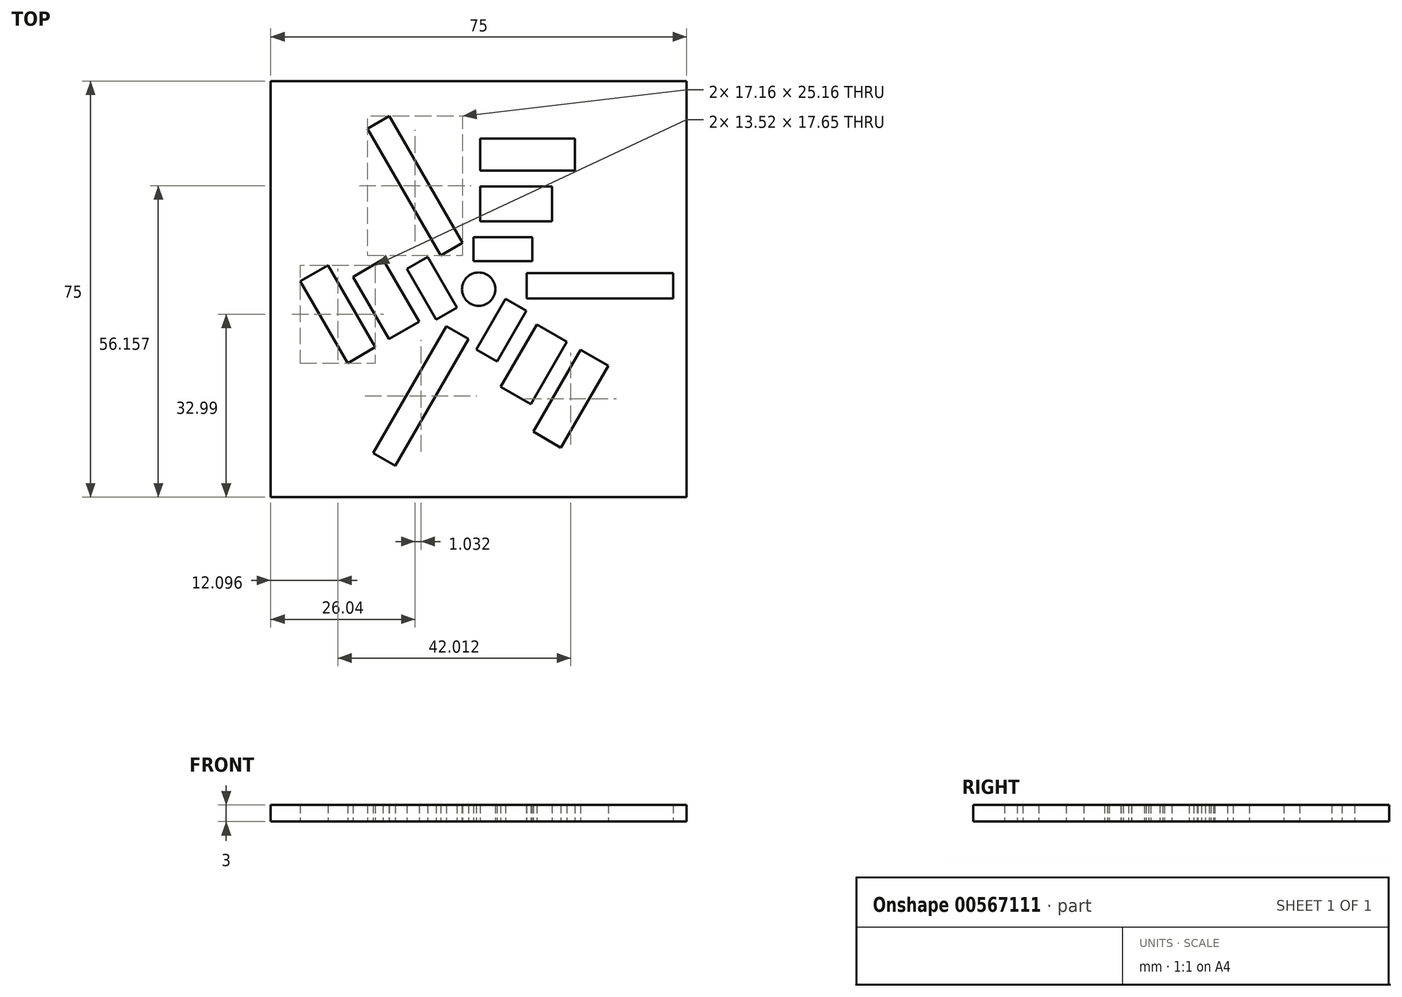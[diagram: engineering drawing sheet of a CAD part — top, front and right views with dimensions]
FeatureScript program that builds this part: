
annotation { "Feature Type Name" : "Feature", "Feature Type Description" : "" }
export const myFeature = defineFeature(function(context is Context, id is Id, definition is map)
    precondition{}
    {
        {
            var Q0;
            Q0=qCreatedBy(makeId("Top.planeOp"),FACE);
            var sketch = newSketch(context, id + "F0", { "sketchPlane" : qUnion([Q0])});
            skLineSegment(sketch, "E0.bottom", {"start": v(0, 0) * mm, "end": v(75, 0) * mm});
            skLineSegment(sketch, "E0.top", {"start": v(0, 75) * mm, "end": v(75, 75) * mm});
            skLineSegment(sketch, "E0.left", {"start": v(0, 0) * mm, "end": v(0, 75) * mm});
            skLineSegment(sketch, "E0.right", {"start": v(75, 0) * mm, "end": v(75, 75) * mm});
            skLineSegment(sketch, "E1", {"start": v(0, 75) * mm, "end": v(75, 0) * mm});
            skCircle(sketch, "E2", {"center": v(37.5, 37.5) * mm, "radius": 7.82 * mm});
            skSolve(sketch);
        }
        {
            var Q0;
            {var subQ1=sQuery(id+"F0.wireOp",EDGE,"E0.bottom");Q0=makeQuery(id+"F0.imprint","IMPRINT",FACE,{"disambiguationData":[TD([[makeQuery(id+"F0.imprint","IMPRINT",EDGE,{"derivedFrom":subQ1}),1.0]])]});}
            var sketch = newSketch(context, id + "F1", { "sketchPlane" : qUnion([Q0])});
            skLineSegment(sketch, "E3.bottom", {"start": v(0, 0) * mm, "end": v(-75, 0) * mm});
            skLineSegment(sketch, "E3.top", {"start": v(0, -75) * mm, "end": v(-75, -75) * mm});
            skLineSegment(sketch, "E3.left", {"start": v(0, 0) * mm, "end": v(0, -75) * mm});
            skLineSegment(sketch, "E3.right", {"start": v(-75, 0) * mm, "end": v(-75, -75) * mm});
            skLineSegment(sketch, "E4", {"start": v(-75, 0) * mm, "end": v(0, -75) * mm});
            skCircle(sketch, "E5", {"center": v(-37.5, -37.5) * mm, "radius": 3 * mm});
            skCircle(sketch, "E6", {"center": v(-37.5, -37.5) * mm, "radius": 37.5 * mm});
            skLineSegment(sketch, "E7.bottom", {"start": v(-38.43, -32.46) * mm, "end": v(-27.86, -32.46) * mm});
            skLineSegment(sketch, "E7.top", {"start": v(-38.43, -28.14) * mm, "end": v(-27.86, -28.14) * mm});
            skLineSegment(sketch, "E7.left", {"start": v(-38.43, -32.46) * mm, "end": v(-38.43, -28.14) * mm});
            skLineSegment(sketch, "E7.right", {"start": v(-27.86, -32.46) * mm, "end": v(-27.86, -28.14) * mm});
            skLineSegment(sketch, "E8.1.0", {"start": v(-45.14, -42.99) * mm, "end": v(-50.43, -33.84) * mm});
            skLineSegment(sketch, "E8.1.1", {"start": v(-46.68, -31.67) * mm, "end": v(-50.43, -33.84) * mm});
            skLineSegment(sketch, "E8.1.2", {"start": v(-41.4, -40.83) * mm, "end": v(-46.68, -31.67) * mm});
            skLineSegment(sketch, "E8.1.3", {"start": v(-41.4, -40.83) * mm, "end": v(-45.14, -42.99) * mm});
            skLineSegment(sketch, "E8.2.0", {"start": v(-28.93, -41.37) * mm, "end": v(-34.2, -50.53) * mm});
            skLineSegment(sketch, "E8.2.1", {"start": v(-37.95, -48.37) * mm, "end": v(-34.2, -50.53) * mm});
            skLineSegment(sketch, "E8.2.2", {"start": v(-32.67, -39.21) * mm, "end": v(-37.95, -48.37) * mm});
            skLineSegment(sketch, "E8.2.3", {"start": v(-32.67, -39.21) * mm, "end": v(-28.93, -41.37) * mm});
            skLineSegment(sketch, "E9.bottom", {"start": v(-37.23, -25.25) * mm, "end": v(-24.26, -25.25) * mm});
            skLineSegment(sketch, "E9.top", {"start": v(-37.23, -19) * mm, "end": v(-24.26, -19) * mm});
            skLineSegment(sketch, "E9.left", {"start": v(-37.23, -25.25) * mm, "end": v(-37.23, -19) * mm});
            skLineSegment(sketch, "E9.right", {"start": v(-24.26, -25.25) * mm, "end": v(-24.26, -19) * mm});
            skLineSegment(sketch, "E10.1.0", {"start": v(-53.65, -46.51) * mm, "end": v(-60.13, -35.28) * mm});
            skLineSegment(sketch, "E10.1.1", {"start": v(-54.72, -32.16) * mm, "end": v(-60.13, -35.28) * mm});
            skLineSegment(sketch, "E10.1.2", {"start": v(-48.24, -43.39) * mm, "end": v(-54.72, -32.16) * mm});
            skLineSegment(sketch, "E10.1.3", {"start": v(-48.24, -43.39) * mm, "end": v(-53.65, -46.51) * mm});
            skLineSegment(sketch, "E10.2.0", {"start": v(-21.62, -46.98) * mm, "end": v(-28.1, -58.21) * mm});
            skLineSegment(sketch, "E10.2.1", {"start": v(-33.52, -55.09) * mm, "end": v(-28.1, -58.21) * mm});
            skLineSegment(sketch, "E10.2.2", {"start": v(-27.03, -43.86) * mm, "end": v(-33.52, -55.09) * mm});
            skLineSegment(sketch, "E10.2.3", {"start": v(-27.03, -43.86) * mm, "end": v(-21.62, -46.98) * mm});
            skLineSegment(sketch, "E11.bottom", {"start": v(-37.23, -16.13) * mm, "end": v(-20.18, -16.13) * mm});
            skLineSegment(sketch, "E11.top", {"start": v(-37.23, -10.36) * mm, "end": v(-20.18, -10.36) * mm});
            skLineSegment(sketch, "E11.left", {"start": v(-37.23, -16.13) * mm, "end": v(-37.23, -10.36) * mm});
            skLineSegment(sketch, "E11.right", {"start": v(-20.18, -16.13) * mm, "end": v(-20.18, -10.36) * mm});
            skLineSegment(sketch, "E12.1.0", {"start": v(-61.14, -50.84) * mm, "end": v(-69.66, -36.07) * mm});
            skLineSegment(sketch, "E12.1.1", {"start": v(-64.67, -33.18) * mm, "end": v(-69.66, -36.07) * mm});
            skLineSegment(sketch, "E12.1.2", {"start": v(-56.14, -47.95) * mm, "end": v(-64.67, -33.18) * mm});
            skLineSegment(sketch, "E12.1.3", {"start": v(-56.14, -47.95) * mm, "end": v(-61.14, -50.84) * mm});
            skLineSegment(sketch, "E12.2.0", {"start": v(-14.13, -51.3) * mm, "end": v(-22.66, -66.07) * mm});
            skLineSegment(sketch, "E12.2.1", {"start": v(-27.65, -63.19) * mm, "end": v(-22.66, -66.07) * mm});
            skLineSegment(sketch, "E12.2.2", {"start": v(-19.12, -48.42) * mm, "end": v(-27.65, -63.19) * mm});
            skLineSegment(sketch, "E12.2.3", {"start": v(-19.12, -48.42) * mm, "end": v(-14.13, -51.3) * mm});
            skLineSegment(sketch, "E13.bottom", {"start": v(-28.82, -34.62) * mm, "end": v(-2.4, -34.62) * mm});
            skLineSegment(sketch, "E13.top", {"start": v(-28.82, -39.19) * mm, "end": v(-2.4, -39.19) * mm});
            skLineSegment(sketch, "E13.left", {"start": v(-28.82, -34.62) * mm, "end": v(-28.82, -39.19) * mm});
            skLineSegment(sketch, "E13.right", {"start": v(-2.4, -34.62) * mm, "end": v(-2.4, -39.19) * mm});
            skLineSegment(sketch, "E14.1.0", {"start": v(-44.33, -31.43) * mm, "end": v(-57.54, -8.54) * mm});
            skLineSegment(sketch, "E14.1.1", {"start": v(-44.33, -31.43) * mm, "end": v(-40.38, -29.14) * mm});
            skLineSegment(sketch, "E14.1.2", {"start": v(-40.38, -29.14) * mm, "end": v(-53.59, -6.26) * mm});
            skLineSegment(sketch, "E14.1.3", {"start": v(-57.54, -8.54) * mm, "end": v(-53.59, -6.26) * mm});
            skLineSegment(sketch, "E14.2.0", {"start": v(-39.35, -46.45) * mm, "end": v(-52.56, -69.33) * mm});
            skLineSegment(sketch, "E14.2.1", {"start": v(-39.35, -46.45) * mm, "end": v(-43.3, -44.17) * mm});
            skLineSegment(sketch, "E14.2.2", {"start": v(-43.3, -44.17) * mm, "end": v(-56.5, -67.05) * mm});
            skLineSegment(sketch, "E14.2.3", {"start": v(-52.56, -69.33) * mm, "end": v(-56.5, -67.05) * mm});
            skSolve(sketch);
        }
        {
            var Q0;
            Q0 = qSketchRegion(id + "F1", true);
            extrude(context, id + "F2", {"entities" : qUnion([Q0]), "depth" : 3 * mm, "offsetDistance" : 25 * mm});
        }
    });
